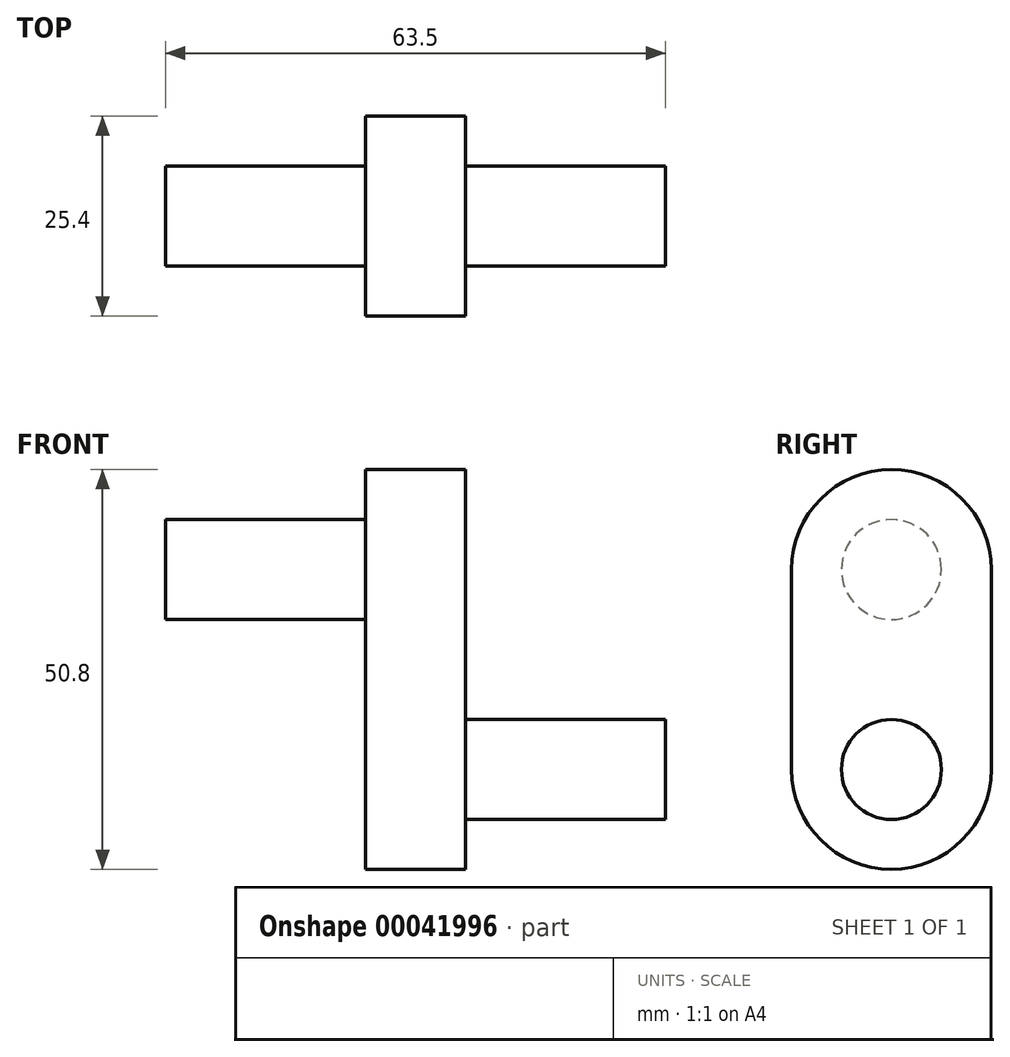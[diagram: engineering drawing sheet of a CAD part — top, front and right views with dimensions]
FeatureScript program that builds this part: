
annotation { "Feature Type Name" : "Feature", "Feature Type Description" : "" }
export const myFeature = defineFeature(function(context is Context, id is Id, definition is map)
    precondition{}
    {
        {
            var Q0;
            Q0=qCreatedBy(makeId("Right.planeOp"),FACE);
            var sketch = newSketch(context, id + "F0", { "sketchPlane" : qUnion([Q0])});
            skCircle(sketch, "E0", {"center": v(0, 0) * mm, "radius": 6.35 * mm});
            skCircle(sketch, "E1", {"center": v(0, 25.4) * mm, "radius": 6.35 * mm});
            skLineSegment(sketch, "E2", {"start": v(0, 25.4) * mm, "end": v(0, 0) * mm});
            skArc(sketch, "E3.0.startCap", {"start": v(-12.7, 25.4) * mm, "mid": v(0, 38.1) * mm, "end": v(12.7, 25.4) * mm});
            skArc(sketch, "E3.0.endCap", {"start": v(12.7, 0) * mm, "mid": v(0, -12.7) * mm, "end": v(-12.7, 0) * mm});
            skLineSegment(sketch, "E3.0.left", {"start": v(12.7, 25.4) * mm, "end": v(12.7, 0) * mm});
            skLineSegment(sketch, "E3.0.right", {"start": v(-12.7, 25.4) * mm, "end": v(-12.7, 0) * mm});
            skSolve(sketch);
        }
        {
            var Q0;
            Q0=makeQuery(id+"F0.imprint","IMPRINT",FACE,{"disambiguationData":[TD([[makeQuery(id+"F0.imprint","IMPRINT",EDGE,{"derivedFrom":sQuery(id+"F0.wireOp",EDGE,"E0")}),-1.0]])]});
            extrude(context, id + "F1", {"entities" : qUnion([Q0]), "depth" : 12.7 * mm});
        }
        {
            var Q0;
            Q0=makeQuery(id+"F0.imprint","IMPRINT",FACE,{"disambiguationData":[TD([[makeQuery(id+"F0.imprint","IMPRINT",EDGE,{"derivedFrom":sQuery(id+"F0.wireOp",EDGE,"E0")}),1.0]])]});
            extrude(context, id + "F2", {"entities" : qUnion([Q0]), "operationType" : NewBodyOperationType.ADD, "depth" : 38.1 * mm});
        }
        {
            var Q0;
            Q0=makeQuery(id+"F0.imprint","IMPRINT",FACE,{"disambiguationData":[TD([[makeQuery(id+"F0.imprint","IMPRINT",EDGE,{"derivedFrom":sQuery(id+"F0.wireOp",EDGE,"E1")}),1.0]])]});
            extrude(context, id + "F3", {"entities" : qUnion([Q0]), "operationType" : NewBodyOperationType.ADD, "oppositeDirection" : true, "depth" : 25.4 * mm, "hasSecondDirection" : true, "secondDirectionOppositeDirection" : false, "secondDirectionDepth" : 12.7 * mm});
        }
    });
